# Revit family: 54-3334-001 DN1400-1800
name_source: partatom
category: Pipe Accessories
units: mm (PartAtom-declared; Revit-internal decimal feet)

## family parameters
Always vertical = No
Cut with Voids When Loaded = No
Part Type = Valve - Breaks Into
Round Connector Dimension = Use Diameter
Shared = No
Work Plane-Based = No

## types (17) — shared parameters
1 = 1 mm  [stored 0.00328084 ft]
10 = 10 mm  [stored 0.0328084 ft]
25 = 25 mm  [stored 0.082021 ft]
54-1400-33-0303100 = DN1400_ PN10_ CTC
54-1400-33-0304100 = DN1400_ PN10_ CTC
54-1400-33-1303100 = DN1400_ PN16_ CTC
54-1400-33-1304100 = DN1400_ PN16_ CTC
54-1400-34-0303100 = DN1400_ PN10_ CTO
54-1400-34-1303100 = DN1400_ PN16_ CTO
54-1600-33-0303100 = DN1600_ PN10_ CTC
54-1600-33-0304100 = DN1600_ PN10_ CTC
54-1600-33-1303100 = DN1600_ PN16_ CTC
54-1600-33-1304100 = DN1600_ PN16_ CTC
54-1600-34-0303100 = DN1600_ PN10_ CTO
54-1600-34-1303100 = DN1600_ PN16_ CTO
54-1600-34-1304100 = DN1600_ PN16_ CTO
54-1800-33-0304100 = DN1800_ PN10_ CTC
54-1800-33-1304100 = DN1800_ PN16_ CTC
54-1800-34-0304100 = DN1800_ PN10_ CTO
54-1800-34-1304100 = DN1800_ PN16_ CTO
60 = 110 mm
Bypass_W = 82 mm
Description_ = AVK GATE VALVE, FLANGED, METAL SEATED, PN10/16
H = 782 mm
Raised_dis = 5 mm  [stored 0.0164042 ft]
Rib_H1 = 600 mm
Search_table = 54-3334-001 DN1400-1800
URL product pages = https://www.avkvalves.com
sweep = 6 mm  [stored 0.019685 ft]
zero-valued in all types: Default Elevation

## per-type parameters (varying)
- 54-1400-33-0303100: ACtuator_T=33.12 mm  [stored 0.108661 ft]; ADN=1400 mm; Actuator_FLR=150 mm; Actuator_angle=133.41 mm; Actuator_dim1=90 mm; Actuator_dim2=54 mm  [stored 0.177165 ft]; BP_centre=50 mm  [stored 0.164042 ft]; BYpass_Bonnet_D1=186.77 mm; BYpass_Bonnet_D2=98.18 mm; Body_H=1435 mm; Body_L=1564.8 mm; Body_T=692.5 mm; Body_W=648 mm; Body_rib_T=18.4 mm  [stored 0.0603675 ft]; Bonnet_FL_L=1956 mm; Bonnet_FL_T=87.4 mm; Bonnet_FL_W=864 mm; Bonnet_dim1=312.96 mm; Bonnet_dim2=226.8 mm; Bonnet_dim3=2468.2 mm; Bonnet_fillet=72 mm; Bonnet_rib_L=978 mm; Bore=700 mm; Bypass_Arc=85 mm; Bypass_DN=100 mm; Bypass_Dimension=194.55 mm; Bypass_H=600 mm; Bypass_H1=60 mm  [stored 0.19685 ft]; Bypass_Location=220 mm; Bypass_R=100 mm; Bypass_R1=200 mm; Bypass_R11=130 mm; Bypass_Stem_D1=540 mm; Bypass_T=25 mm  [stored 0.082021 ft]; Bypass_Valve_Location=1102.45 mm; Bypass_cap=856.02 mm; Bypass_dis=50 mm  [stored 0.164042 ft]; Bypass_shaft=140 mm; Bypass_stem_D2=33.12 mm  [stored 0.108661 ft]; Bypass_stem_D3=52.99 mm; Bypass_valve_FL1=115.5 mm; Bypass_valve_FL2=155.93 mm; Bypass_valve_L1=320 mm; Bypass_valve_L2=116.73 mm; Bypass_valve_L3=175.1 mm; Bypass_valve_T=77 mm; Bypass_valve_W=155.64 mm; Cut_dis=43.7 mm  [stored 0.143373 ft]; DN=1400 mm; F=60 mm  [stored 0.19685 ft]; F1=27 mm  [stored 0.0885827 ft]; F2=166 mm; FL_T=46 mm  [stored 0.150919 ft]; Fillet=216 mm; H1=2870 mm; H2=885 mm; L=876 mm; OD=1675 mm; OD1=1770 mm; PN=10 mm  [stored 0.0328084 ft]; Raised_dia=1530 mm; Rib_Actual=1137.5 mm; Rib_H=1148 mm; Rib_H2=950 mm; Rib_H3=1150 mm; Rib_H4=1310 mm; Rib_L=880.2 mm; Rib_W=388.8 mm; Stem_dim=75 mm; W=2275 mm; W1=1297 mm; W_half=978 mm; bottom_rib=837.5 mm; stem_dim=55.33 mm; stem_dim1=97.5 mm; wedge_dim1=712.8 mm
- 54-1400-33-0304100: ACtuator_T=33.12 mm  [stored 0.108661 ft]; ADN=1400 mm; Actuator_FLR=175 mm; Actuator_angle=133.41 mm; Actuator_dim1=105 mm; Actuator_dim2=63 mm  [stored 0.206693 ft]; BP_centre=50 mm  [stored 0.164042 ft]; BYpass_Bonnet_D1=186.77 mm; BYpass_Bonnet_D2=98.18 mm; Body_H=1435 mm; Body_L=1564.8 mm; Body_T=692.5 mm; Body_W=648 mm; Body_rib_T=18.4 mm  [stored 0.0603675 ft]; Bonnet_FL_L=1956 mm; Bonnet_FL_T=87.4 mm; Bonnet_FL_W=864 mm; Bonnet_dim1=312.96 mm; Bonnet_dim2=226.8 mm; Bonnet_dim3=2468.2 mm; Bonnet_fillet=72 mm; Bonnet_rib_L=978 mm; Bore=700.05 mm; Bypass_Arc=85 mm; Bypass_DN=100 mm; Bypass_Dimension=194.55 mm; Bypass_H=600 mm; Bypass_H1=60 mm  [stored 0.19685 ft]; Bypass_Location=220 mm; Bypass_R=100 mm; Bypass_R1=200 mm; Bypass_R11=130 mm; Bypass_Stem_D1=540 mm; Bypass_T=25 mm  [stored 0.082021 ft]; Bypass_Valve_Location=1102.45 mm; Bypass_cap=856.02 mm; Bypass_dis=50 mm  [stored 0.164042 ft]; Bypass_shaft=140 mm; Bypass_stem_D2=33.12 mm  [stored 0.108661 ft]; Bypass_stem_D3=52.99 mm; Bypass_valve_FL1=115.5 mm; Bypass_valve_FL2=155.93 mm; Bypass_valve_L1=320 mm; Bypass_valve_L2=116.73 mm; Bypass_valve_L3=175.1 mm; Bypass_valve_T=77 mm; Bypass_valve_W=155.64 mm; Cut_dis=43.7 mm  [stored 0.143373 ft]; DN=1400.1 mm; F=70 mm; F1=31.5 mm  [stored 0.103346 ft]; F2=202 mm; FL_T=46 mm  [stored 0.150919 ft]; Fillet=216 mm; H1=2870 mm; H2=885 mm; L=876 mm; OD=1675 mm; OD1=1770 mm; PN=10 mm  [stored 0.0328084 ft]; Raised_dia=1530 mm; Rib_Actual=1137.5 mm; Rib_H=1148 mm; Rib_H2=950 mm; Rib_H3=1150 mm; Rib_H4=1310 mm; Rib_L=880.2 mm; Rib_W=388.8 mm; Stem_dim=87.5 mm; W=2275 mm; W1=1297 mm; W_half=978 mm; bottom_rib=837.5 mm; stem_dim=67.33 mm; stem_dim1=113.75 mm; wedge_dim1=712.8 mm
- 54-1400-33-1303100: ACtuator_T=43.2 mm  [stored 0.141732 ft]; ADN=1400 mm; Actuator_FLR=150 mm; Actuator_angle=133.41 mm; Actuator_dim1=90 mm; Actuator_dim2=54 mm  [stored 0.177165 ft]; BP_centre=50 mm  [stored 0.164042 ft]; BYpass_Bonnet_D1=186.77 mm; BYpass_Bonnet_D2=98.18 mm; Body_H=1435 mm; Body_L=1564.8 mm; Body_T=692.5 mm; Body_W=648 mm; Body_rib_T=24 mm  [stored 0.0787402 ft]; Bonnet_FL_L=1956 mm; Bonnet_FL_T=114 mm; Bonnet_FL_W=864 mm; Bonnet_dim1=312.96 mm; Bonnet_dim2=226.8 mm; Bonnet_dim3=2468.2 mm; Bonnet_fillet=72 mm; Bonnet_rib_L=978 mm; Bore=700.06 mm; Bypass_Arc=85 mm; Bypass_DN=100 mm; Bypass_Dimension=194.55 mm; Bypass_H=600 mm; Bypass_H1=60 mm  [stored 0.19685 ft]; Bypass_Location=220 mm; Bypass_R=100 mm; Bypass_R1=200 mm; Bypass_R11=130 mm; Bypass_Stem_D1=540 mm; Bypass_T=25 mm  [stored 0.082021 ft]; Bypass_Valve_Location=1102.45 mm; Bypass_cap=856.02 mm; Bypass_dis=50 mm  [stored 0.164042 ft]; Bypass_shaft=140 mm; Bypass_stem_D2=43.2 mm  [stored 0.141732 ft]; Bypass_stem_D3=69.12 mm; Bypass_valve_FL1=115.5 mm; Bypass_valve_FL2=155.93 mm; Bypass_valve_L1=320 mm; Bypass_valve_L2=116.73 mm; Bypass_valve_L3=175.1 mm; Bypass_valve_T=77 mm; Bypass_valve_W=155.64 mm; Cut_dis=57 mm  [stored 0.187008 ft]; DN=1400.11 mm; F=60 mm  [stored 0.19685 ft]; F1=27 mm  [stored 0.0885827 ft]; F2=166 mm; FL_T=60 mm  [stored 0.19685 ft]; Fillet=216 mm; H1=2870 mm; H2=885 mm; L=876 mm; OD=1675 mm; OD1=1770 mm; PN=16 mm  [stored 0.0524934 ft]; Raised_dia=1530 mm; Rib_Actual=1137.5 mm; Rib_H=1148 mm; Rib_H2=950 mm; Rib_H3=1150 mm; Rib_H4=1310 mm; Rib_L=880.2 mm; Rib_W=388.8 mm; Stem_dim=75 mm; W=2275 mm; W1=1297 mm; W_half=978 mm; bottom_rib=837.5 mm; stem_dim=55.33 mm; stem_dim1=97.5 mm; wedge_dim1=712.8 mm
- 54-1400-33-1304100: ACtuator_T=43.2 mm  [stored 0.141732 ft]; ADN=1400 mm; Actuator_FLR=175 mm; Actuator_angle=133.41 mm; Actuator_dim1=105 mm; Actuator_dim2=63 mm  [stored 0.206693 ft]; BP_centre=50 mm  [stored 0.164042 ft]; BYpass_Bonnet_D1=186.77 mm; BYpass_Bonnet_D2=98.18 mm; Body_H=1435 mm; Body_L=1564.8 mm; Body_T=692.5 mm; Body_W=648 mm; Body_rib_T=24 mm  [stored 0.0787402 ft]; Bonnet_FL_L=1956 mm; Bonnet_FL_T=114 mm; Bonnet_FL_W=864 mm; Bonnet_dim1=312.96 mm; Bonnet_dim2=226.8 mm; Bonnet_dim3=2468.2 mm; Bonnet_fillet=72 mm; Bonnet_rib_L=978 mm; Bore=700.06 mm; Bypass_Arc=85 mm; Bypass_DN=100 mm; Bypass_Dimension=194.55 mm; Bypass_H=600 mm; Bypass_H1=60 mm  [stored 0.19685 ft]; Bypass_Location=220 mm; Bypass_R=100 mm; Bypass_R1=200 mm; Bypass_R11=130 mm; Bypass_Stem_D1=540 mm; Bypass_T=25 mm  [stored 0.082021 ft]; Bypass_Valve_Location=1102.45 mm; Bypass_cap=856.02 mm; Bypass_dis=50 mm  [stored 0.164042 ft]; Bypass_shaft=140 mm; Bypass_stem_D2=43.2 mm  [stored 0.141732 ft]; Bypass_stem_D3=69.12 mm; Bypass_valve_FL1=115.5 mm; Bypass_valve_FL2=155.93 mm; Bypass_valve_L1=320 mm; Bypass_valve_L2=116.73 mm; Bypass_valve_L3=175.1 mm; Bypass_valve_T=77 mm; Bypass_valve_W=155.64 mm; Cut_dis=57 mm  [stored 0.187008 ft]; DN=1400.12 mm; F=70 mm; F1=31.5 mm  [stored 0.103346 ft]; F2=202 mm; FL_T=60 mm  [stored 0.19685 ft]; Fillet=216 mm; H1=2870 mm; H2=885 mm; L=876 mm; OD=1675 mm; OD1=1770 mm; PN=16 mm  [stored 0.0524934 ft]; Raised_dia=1530 mm; Rib_Actual=1137.5 mm; Rib_H=1148 mm; Rib_H2=950 mm; Rib_H3=1150 mm; Rib_H4=1310 mm; Rib_L=880.2 mm; Rib_W=388.8 mm; Stem_dim=87.5 mm; W=2275 mm; W1=1297 mm; W_half=978 mm; bottom_rib=837.5 mm; stem_dim=67.33 mm; stem_dim1=113.75 mm; wedge_dim1=712.8 mm
- 54-1400-34-0303100: ACtuator_T=33.12 mm  [stored 0.108661 ft]; ADN=1400 mm; Actuator_FLR=150 mm; Actuator_angle=133.41 mm; Actuator_dim1=90 mm; Actuator_dim2=54 mm  [stored 0.177165 ft]; BP_centre=50 mm  [stored 0.164042 ft]; BYpass_Bonnet_D1=186.77 mm; BYpass_Bonnet_D2=98.18 mm; Body_H=1435 mm; Body_L=1564.8 mm; Body_T=692.5 mm; Body_W=648 mm; Body_rib_T=18.4 mm  [stored 0.0603675 ft]; Bonnet_FL_L=1956 mm; Bonnet_FL_T=87.4 mm; Bonnet_FL_W=864 mm; Bonnet_dim1=312.96 mm; Bonnet_dim2=226.8 mm; Bonnet_dim3=2468.2 mm; Bonnet_fillet=72 mm; Bonnet_rib_L=978 mm; Bore=700.07 mm; Bypass_Arc=85 mm; Bypass_DN=100 mm; Bypass_Dimension=194.55 mm; Bypass_H=600 mm; Bypass_H1=60 mm  [stored 0.19685 ft]; Bypass_Location=220 mm; Bypass_R=100 mm; Bypass_R1=200 mm; Bypass_R11=130 mm; Bypass_Stem_D1=540 mm; Bypass_T=25 mm  [stored 0.082021 ft]; Bypass_Valve_Location=1102.45 mm; Bypass_cap=856.02 mm; Bypass_dis=50 mm  [stored 0.164042 ft]; Bypass_shaft=140 mm; Bypass_stem_D2=33.12 mm  [stored 0.108661 ft]; Bypass_stem_D3=52.99 mm; Bypass_valve_FL1=115.5 mm; Bypass_valve_FL2=155.93 mm; Bypass_valve_L1=320 mm; Bypass_valve_L2=116.73 mm; Bypass_valve_L3=175.1 mm; Bypass_valve_T=77 mm; Bypass_valve_W=155.64 mm; Cut_dis=43.7 mm  [stored 0.143373 ft]; DN=1400.13 mm; F=60 mm  [stored 0.19685 ft]; F1=27 mm  [stored 0.0885827 ft]; F2=166 mm; FL_T=46 mm  [stored 0.150919 ft]; Fillet=216 mm; H1=2870 mm; H2=885 mm; L=876 mm; OD=1675 mm; OD1=1770 mm; PN=10 mm  [stored 0.0328084 ft]; Raised_dia=1530 mm; Rib_Actual=1137.5 mm; Rib_H=1148 mm; Rib_H2=950 mm; Rib_H3=1150 mm; Rib_H4=1310 mm; Rib_L=880.2 mm; Rib_W=388.8 mm; Stem_dim=75 mm; W=2275 mm; W1=1297 mm; W_half=978 mm; bottom_rib=837.5 mm; stem_dim=55.33 mm; stem_dim1=97.5 mm; wedge_dim1=712.8 mm
- 54-1400-34-1303100: ACtuator_T=43.2 mm  [stored 0.141732 ft]; ADN=1400 mm; Actuator_FLR=150 mm; Actuator_angle=133.41 mm; Actuator_dim1=90 mm; Actuator_dim2=54 mm  [stored 0.177165 ft]; BP_centre=50 mm  [stored 0.164042 ft]; BYpass_Bonnet_D1=186.77 mm; BYpass_Bonnet_D2=98.18 mm; Body_H=1435 mm; Body_L=1564.8 mm; Body_T=692.5 mm; Body_W=648 mm; Body_rib_T=24 mm  [stored 0.0787402 ft]; Bonnet_FL_L=1956 mm; Bonnet_FL_T=114 mm; Bonnet_FL_W=864 mm; Bonnet_dim1=312.96 mm; Bonnet_dim2=226.8 mm; Bonnet_dim3=2468.2 mm; Bonnet_fillet=72 mm; Bonnet_rib_L=978 mm; Bore=700.07 mm; Bypass_Arc=85 mm; Bypass_DN=100 mm; Bypass_Dimension=194.55 mm; Bypass_H=600 mm; Bypass_H1=60 mm  [stored 0.19685 ft]; Bypass_Location=220 mm; Bypass_R=100 mm; Bypass_R1=200 mm; Bypass_R11=130 mm; Bypass_Stem_D1=540 mm; Bypass_T=25 mm  [stored 0.082021 ft]; Bypass_Valve_Location=1102.45 mm; Bypass_cap=856.02 mm; Bypass_dis=50 mm  [stored 0.164042 ft]; Bypass_shaft=140 mm; Bypass_stem_D2=43.2 mm  [stored 0.141732 ft]; Bypass_stem_D3=69.12 mm; Bypass_valve_FL1=115.5 mm; Bypass_valve_FL2=155.93 mm; Bypass_valve_L1=320 mm; Bypass_valve_L2=116.73 mm; Bypass_valve_L3=175.1 mm; Bypass_valve_T=77 mm; Bypass_valve_W=155.64 mm; Cut_dis=57 mm  [stored 0.187008 ft]; DN=1400.14 mm; F=60 mm  [stored 0.19685 ft]; F1=27 mm  [stored 0.0885827 ft]; F2=166 mm; FL_T=60 mm  [stored 0.19685 ft]; Fillet=216 mm; H1=2870 mm; H2=885 mm; L=876 mm; OD=1675 mm; OD1=1770 mm; PN=16 mm  [stored 0.0524934 ft]; Raised_dia=1530 mm; Rib_Actual=1137.5 mm; Rib_H=1148 mm; Rib_H2=950 mm; Rib_H3=1150 mm; Rib_H4=1310 mm; Rib_L=880.2 mm; Rib_W=388.8 mm; Stem_dim=75 mm; W=2275 mm; W1=1297 mm; W_half=978 mm; bottom_rib=837.5 mm; stem_dim=55.33 mm; stem_dim1=97.5 mm; wedge_dim1=712.8 mm
- 54-1600-33-0303100: ACtuator_T=35.28 mm  [stored 0.115748 ft]; ADN=1600 mm; Actuator_FLR=150 mm; Actuator_angle=141.13 mm; Actuator_dim1=90 mm; Actuator_dim2=54 mm  [stored 0.177165 ft]; BP_centre=65 mm; BYpass_Bonnet_D1=206.5 mm; BYpass_Bonnet_D2=115.58 mm; Body_H=1645.5 mm; Body_L=1832 mm; Body_T=792.5 mm; Body_W=685.5 mm; Body_rib_T=19.6 mm  [stored 0.0643045 ft]; Bonnet_FL_L=2290 mm; Bonnet_FL_T=93.1 mm; Bonnet_FL_W=914 mm; Bonnet_dim1=366.4 mm; Bonnet_dim2=239.93 mm; Bonnet_dim3=2830.26 mm; Bonnet_fillet=76.17 mm; Bonnet_rib_L=1145 mm; Bore=800 mm; Bypass_Arc=100 mm; Bypass_DN=150 mm; Bypass_Dimension=215.1 mm; Bypass_H=730 mm; Bypass_H1=73 mm; Bypass_Location=259 mm; Bypass_R=130 mm; Bypass_R1=260 mm; Bypass_R11=169 mm; Bypass_Stem_D1=657 mm; Bypass_T=35 mm  [stored 0.114829 ft]; Bypass_Valve_Location=1218.9 mm; Bypass_cap=946.44 mm; Bypass_dis=60 mm  [stored 0.19685 ft]; Bypass_shaft=150 mm; Bypass_stem_D2=35.28 mm  [stored 0.115748 ft]; Bypass_stem_D3=56.45 mm; Bypass_valve_FL1=135.98 mm; Bypass_valve_FL2=183.57 mm; Bypass_valve_L1=360 mm; Bypass_valve_L2=129.06 mm; Bypass_valve_L3=193.59 mm; Bypass_valve_T=90.65 mm; Bypass_valve_W=172.08 mm; Cut_dis=46.55 mm  [stored 0.152723 ft]; DN=1600 mm; F=60 mm  [stored 0.19685 ft]; F1=27 mm  [stored 0.0885827 ft]; F2=179 mm; FL_T=49 mm  [stored 0.160761 ft]; Fillet=228.5 mm; H1=3291 mm; H2=1060 mm; L=914 mm; OD=1915 mm; OD1=2120 mm; PN=10 mm  [stored 0.0328084 ft]; Raised_dia=1750 mm; Rib_Actual=1288.5 mm; Rib_H=1316.4 mm; Rib_H2=1100 mm; Rib_H3=1300 mm; Rib_H4=1500 mm; Rib_L=1030.5 mm; Rib_W=411.3 mm; Stem_dim=75 mm; W=2577 mm; W1=1434 mm; W_half=1143 mm; bottom_rib=957.5 mm; stem_dim=59.67 mm; stem_dim1=97.5 mm; wedge_dim1=754.05 mm
- 54-1600-33-0304100: ACtuator_T=35.28 mm  [stored 0.115748 ft]; ADN=1600 mm; Actuator_FLR=175 mm; Actuator_angle=141.13 mm; Actuator_dim1=105 mm; Actuator_dim2=63 mm  [stored 0.206693 ft]; BP_centre=65 mm; BYpass_Bonnet_D1=206.5 mm; BYpass_Bonnet_D2=115.58 mm; Body_H=1645.5 mm; Body_L=1832 mm; Body_T=792.5 mm; Body_W=685.5 mm; Body_rib_T=19.6 mm  [stored 0.0643045 ft]; Bonnet_FL_L=2290 mm; Bonnet_FL_T=93.1 mm; Bonnet_FL_W=914 mm; Bonnet_dim1=366.4 mm; Bonnet_dim2=239.93 mm; Bonnet_dim3=2830.26 mm; Bonnet_fillet=76.17 mm; Bonnet_rib_L=1145 mm; Bore=800.05 mm; Bypass_Arc=100 mm; Bypass_DN=150 mm; Bypass_Dimension=215.1 mm; Bypass_H=730 mm; Bypass_H1=73 mm; Bypass_Location=259 mm; Bypass_R=130 mm; Bypass_R1=260 mm; Bypass_R11=169 mm; Bypass_Stem_D1=657 mm; Bypass_T=35 mm  [stored 0.114829 ft]; Bypass_Valve_Location=1218.9 mm; Bypass_cap=946.44 mm; Bypass_dis=60 mm  [stored 0.19685 ft]; Bypass_shaft=150 mm; Bypass_stem_D2=35.28 mm  [stored 0.115748 ft]; Bypass_stem_D3=56.45 mm; Bypass_valve_FL1=135.98 mm; Bypass_valve_FL2=183.57 mm; Bypass_valve_L1=360 mm; Bypass_valve_L2=129.06 mm; Bypass_valve_L3=193.59 mm; Bypass_valve_T=90.65 mm; Bypass_valve_W=172.08 mm; Cut_dis=46.55 mm  [stored 0.152723 ft]; DN=1600.1 mm; F=70 mm; F1=31.5 mm  [stored 0.103346 ft]; F2=205 mm; FL_T=49 mm  [stored 0.160761 ft]; Fillet=228.5 mm; H1=3291 mm; H2=1060 mm; L=914 mm; OD=1915 mm; OD1=2120 mm; PN=10 mm  [stored 0.0328084 ft]; Raised_dia=1750 mm; Rib_Actual=1288.5 mm; Rib_H=1316.4 mm; Rib_H2=1100 mm; Rib_H3=1300 mm; Rib_H4=1500 mm; Rib_L=1030.5 mm; Rib_W=411.3 mm; Stem_dim=87.5 mm; W=2577 mm; W1=1434 mm; W_half=1143 mm; bottom_rib=957.5 mm; stem_dim=68.33 mm; stem_dim1=113.75 mm; wedge_dim1=754.05 mm
- 54-1600-33-1303100: ACtuator_T=46.8 mm  [stored 0.153543 ft]; ADN=1600 mm; Actuator_FLR=150 mm; Actuator_angle=141.13 mm; Actuator_dim1=90 mm; Actuator_dim2=54 mm  [stored 0.177165 ft]; BP_centre=65 mm; BYpass_Bonnet_D1=206.5 mm; BYpass_Bonnet_D2=115.58 mm; Body_H=1645.5 mm; Body_L=1832 mm; Body_T=792.5 mm; Body_W=685.5 mm; Body_rib_T=26 mm; Bonnet_FL_L=2290 mm; Bonnet_FL_T=123.5 mm; Bonnet_FL_W=914 mm; Bonnet_dim1=366.4 mm; Bonnet_dim2=239.93 mm; Bonnet_dim3=2830.26 mm; Bonnet_fillet=76.17 mm; Bonnet_rib_L=1145 mm; Bore=800.06 mm; Bypass_Arc=100 mm; Bypass_DN=150 mm; Bypass_Dimension=215.1 mm; Bypass_H=730 mm; Bypass_H1=73 mm; Bypass_Location=259 mm; Bypass_R=130 mm; Bypass_R1=260 mm; Bypass_R11=169 mm; Bypass_Stem_D1=657 mm; Bypass_T=35 mm  [stored 0.114829 ft]; Bypass_Valve_Location=1218.9 mm; Bypass_cap=946.44 mm; Bypass_dis=60 mm  [stored 0.19685 ft]; Bypass_shaft=150 mm; Bypass_stem_D2=46.8 mm  [stored 0.153543 ft]; Bypass_stem_D3=74.88 mm; Bypass_valve_FL1=135.98 mm; Bypass_valve_FL2=183.57 mm; Bypass_valve_L1=360 mm; Bypass_valve_L2=129.06 mm; Bypass_valve_L3=193.59 mm; Bypass_valve_T=90.65 mm; Bypass_valve_W=172.08 mm; Cut_dis=61.75 mm; DN=1600.11 mm; F=60 mm  [stored 0.19685 ft]; F1=27 mm  [stored 0.0885827 ft]; F2=179 mm; FL_T=65 mm; Fillet=228.5 mm; H1=3291 mm; H2=1060 mm; L=914 mm; OD=1915 mm; OD1=2120 mm; PN=16 mm  [stored 0.0524934 ft]; Raised_dia=1750 mm; Rib_Actual=1288.5 mm; Rib_H=1316.4 mm; Rib_H2=1100 mm; Rib_H3=1300 mm; Rib_H4=1500 mm; Rib_L=1030.5 mm; Rib_W=411.3 mm; Stem_dim=75 mm; W=2577 mm; W1=1434 mm; W_half=1143 mm; bottom_rib=957.5 mm; stem_dim=59.67 mm; stem_dim1=97.5 mm; wedge_dim1=754.05 mm
- 54-1600-33-1304100: ACtuator_T=46.8 mm  [stored 0.153543 ft]; ADN=1600 mm; Actuator_FLR=175 mm; Actuator_angle=141.13 mm; Actuator_dim1=105 mm; Actuator_dim2=63 mm  [stored 0.206693 ft]; BP_centre=65 mm; BYpass_Bonnet_D1=206.5 mm; BYpass_Bonnet_D2=115.58 mm; Body_H=1645.5 mm; Body_L=1832 mm; Body_T=792.5 mm; Body_W=685.5 mm; Body_rib_T=26 mm; Bonnet_FL_L=2290 mm; Bonnet_FL_T=123.5 mm; Bonnet_FL_W=914 mm; Bonnet_dim1=366.4 mm; Bonnet_dim2=239.93 mm; Bonnet_dim3=2830.26 mm; Bonnet_fillet=76.17 mm; Bonnet_rib_L=1145 mm; Bore=800.06 mm; Bypass_Arc=100 mm; Bypass_DN=150 mm; Bypass_Dimension=215.1 mm; Bypass_H=730 mm; Bypass_H1=73 mm; Bypass_Location=259 mm; Bypass_R=130 mm; Bypass_R1=260 mm; Bypass_R11=169 mm; Bypass_Stem_D1=657 mm; Bypass_T=35 mm  [stored 0.114829 ft]; Bypass_Valve_Location=1218.9 mm; Bypass_cap=946.44 mm; Bypass_dis=60 mm  [stored 0.19685 ft]; Bypass_shaft=150 mm; Bypass_stem_D2=46.8 mm  [stored 0.153543 ft]; Bypass_stem_D3=74.88 mm; Bypass_valve_FL1=135.98 mm; Bypass_valve_FL2=183.57 mm; Bypass_valve_L1=360 mm; Bypass_valve_L2=129.06 mm; Bypass_valve_L3=193.59 mm; Bypass_valve_T=90.65 mm; Bypass_valve_W=172.08 mm; Cut_dis=61.75 mm; DN=1600.12 mm; F=70 mm; F1=31.5 mm  [stored 0.103346 ft]; F2=205 mm; FL_T=65 mm; Fillet=228.5 mm; H1=3291 mm; H2=1060 mm; L=914 mm; OD=1915 mm; OD1=2120 mm; PN=16 mm  [stored 0.0524934 ft]; Raised_dia=1750 mm; Rib_Actual=1288.5 mm; Rib_H=1316.4 mm; Rib_H2=1100 mm; Rib_H3=1300 mm; Rib_H4=1500 mm; Rib_L=1030.5 mm; Rib_W=411.3 mm; Stem_dim=87.5 mm; W=2577 mm; W1=1434 mm; W_half=1143 mm; bottom_rib=957.5 mm; stem_dim=68.33 mm; stem_dim1=113.75 mm; wedge_dim1=754.05 mm
- 54-1600-34-0303100: ACtuator_T=35.28 mm  [stored 0.115748 ft]; ADN=1600 mm; Actuator_FLR=150 mm; Actuator_angle=141.13 mm; Actuator_dim1=90 mm; Actuator_dim2=54 mm  [stored 0.177165 ft]; BP_centre=65 mm; BYpass_Bonnet_D1=206.5 mm; BYpass_Bonnet_D2=115.58 mm; Body_H=1645.5 mm; Body_L=1832 mm; Body_T=792.5 mm; Body_W=685.5 mm; Body_rib_T=19.6 mm  [stored 0.0643045 ft]; Bonnet_FL_L=2290 mm; Bonnet_FL_T=93.1 mm; Bonnet_FL_W=914 mm; Bonnet_dim1=366.4 mm; Bonnet_dim2=239.93 mm; Bonnet_dim3=2830.26 mm; Bonnet_fillet=76.17 mm; Bonnet_rib_L=1145 mm; Bore=800.07 mm; Bypass_Arc=100 mm; Bypass_DN=150 mm; Bypass_Dimension=215.1 mm; Bypass_H=730 mm; Bypass_H1=73 mm; Bypass_Location=259 mm; Bypass_R=130 mm; Bypass_R1=260 mm; Bypass_R11=169 mm; Bypass_Stem_D1=657 mm; Bypass_T=35 mm  [stored 0.114829 ft]; Bypass_Valve_Location=1218.9 mm; Bypass_cap=946.44 mm; Bypass_dis=60 mm  [stored 0.19685 ft]; Bypass_shaft=150 mm; Bypass_stem_D2=35.28 mm  [stored 0.115748 ft]; Bypass_stem_D3=56.45 mm; Bypass_valve_FL1=135.98 mm; Bypass_valve_FL2=183.57 mm; Bypass_valve_L1=360 mm; Bypass_valve_L2=129.06 mm; Bypass_valve_L3=193.59 mm; Bypass_valve_T=90.65 mm; Bypass_valve_W=172.08 mm; Cut_dis=46.55 mm  [stored 0.152723 ft]; DN=1600.13 mm; F=60 mm  [stored 0.19685 ft]; F1=27 mm  [stored 0.0885827 ft]; F2=179 mm; FL_T=49 mm  [stored 0.160761 ft]; Fillet=228.5 mm; H1=3291 mm; H2=1060 mm; L=914 mm; OD=1915 mm; OD1=2120 mm; PN=10 mm  [stored 0.0328084 ft]; Raised_dia=1750 mm; Rib_Actual=1288.5 mm; Rib_H=1316.4 mm; Rib_H2=1100 mm; Rib_H3=1300 mm; Rib_H4=1500 mm; Rib_L=1030.5 mm; Rib_W=411.3 mm; Stem_dim=75 mm; W=2577 mm; W1=1434 mm; W_half=1143 mm; bottom_rib=957.5 mm; stem_dim=59.67 mm; stem_dim1=97.5 mm; wedge_dim1=754.05 mm
- 54-1600-34-1303100: ACtuator_T=46.8 mm  [stored 0.153543 ft]; ADN=1600 mm; Actuator_FLR=150 mm; Actuator_angle=141.13 mm; Actuator_dim1=90 mm; Actuator_dim2=54 mm  [stored 0.177165 ft]; BP_centre=65 mm; BYpass_Bonnet_D1=206.5 mm; BYpass_Bonnet_D2=115.58 mm; Body_H=1645.5 mm; Body_L=1832 mm; Body_T=792.5 mm; Body_W=685.5 mm; Body_rib_T=26 mm; Bonnet_FL_L=2290 mm; Bonnet_FL_T=123.5 mm; Bonnet_FL_W=914 mm; Bonnet_dim1=366.4 mm; Bonnet_dim2=239.93 mm; Bonnet_dim3=2830.26 mm; Bonnet_fillet=76.17 mm; Bonnet_rib_L=1145 mm; Bore=800.07 mm; Bypass_Arc=100 mm; Bypass_DN=150 mm; Bypass_Dimension=215.1 mm; Bypass_H=730 mm; Bypass_H1=73 mm; Bypass_Location=259 mm; Bypass_R=130 mm; Bypass_R1=260 mm; Bypass_R11=169 mm; Bypass_Stem_D1=657 mm; Bypass_T=35 mm  [stored 0.114829 ft]; Bypass_Valve_Location=1218.9 mm; Bypass_cap=946.44 mm; Bypass_dis=60 mm  [stored 0.19685 ft]; Bypass_shaft=150 mm; Bypass_stem_D2=46.8 mm  [stored 0.153543 ft]; Bypass_stem_D3=74.88 mm; Bypass_valve_FL1=135.98 mm; Bypass_valve_FL2=183.57 mm; Bypass_valve_L1=360 mm; Bypass_valve_L2=129.06 mm; Bypass_valve_L3=193.59 mm; Bypass_valve_T=90.65 mm; Bypass_valve_W=172.08 mm; Cut_dis=61.75 mm; DN=1600.14 mm; F=60 mm  [stored 0.19685 ft]; F1=27 mm  [stored 0.0885827 ft]; F2=179 mm; FL_T=65 mm; Fillet=228.5 mm; H1=3291 mm; H2=1060 mm; L=914 mm; OD=1915 mm; OD1=2120 mm; PN=16 mm  [stored 0.0524934 ft]; Raised_dia=1750 mm; Rib_Actual=1288.5 mm; Rib_H=1316.4 mm; Rib_H2=1100 mm; Rib_H3=1300 mm; Rib_H4=1500 mm; Rib_L=1030.5 mm; Rib_W=411.3 mm; Stem_dim=75 mm; W=2577 mm; W1=1434 mm; W_half=1143 mm; bottom_rib=957.5 mm; stem_dim=59.67 mm; stem_dim1=97.5 mm; wedge_dim1=754.05 mm
- 54-1600-34-1304100: ACtuator_T=46.8 mm  [stored 0.153543 ft]; ADN=1600 mm; Actuator_FLR=175 mm; Actuator_angle=141.13 mm; Actuator_dim1=105 mm; Actuator_dim2=63 mm  [stored 0.206693 ft]; BP_centre=65 mm; BYpass_Bonnet_D1=206.5 mm; BYpass_Bonnet_D2=115.58 mm; Body_H=1645.5 mm; Body_L=1832 mm; Body_T=792.5 mm; Body_W=685.5 mm; Body_rib_T=26 mm; Bonnet_FL_L=2290 mm; Bonnet_FL_T=123.5 mm; Bonnet_FL_W=914 mm; Bonnet_dim1=366.4 mm; Bonnet_dim2=239.93 mm; Bonnet_dim3=2830.26 mm; Bonnet_fillet=76.17 mm; Bonnet_rib_L=1145 mm; Bore=800.08 mm; Bypass_Arc=100 mm; Bypass_DN=150 mm; Bypass_Dimension=215.1 mm; Bypass_H=730 mm; Bypass_H1=73 mm; Bypass_Location=259 mm; Bypass_R=130 mm; Bypass_R1=260 mm; Bypass_R11=169 mm; Bypass_Stem_D1=657 mm; Bypass_T=35 mm  [stored 0.114829 ft]; Bypass_Valve_Location=1218.9 mm; Bypass_cap=946.44 mm; Bypass_dis=60 mm  [stored 0.19685 ft]; Bypass_shaft=150 mm; Bypass_stem_D2=46.8 mm  [stored 0.153543 ft]; Bypass_stem_D3=74.88 mm; Bypass_valve_FL1=135.98 mm; Bypass_valve_FL2=183.57 mm; Bypass_valve_L1=360 mm; Bypass_valve_L2=129.06 mm; Bypass_valve_L3=193.59 mm; Bypass_valve_T=90.65 mm; Bypass_valve_W=172.08 mm; Cut_dis=61.75 mm; DN=1600.15 mm; F=70 mm; F1=31.5 mm  [stored 0.103346 ft]; F2=205 mm; FL_T=65 mm; Fillet=228.5 mm; H1=3291 mm; H2=1060 mm; L=914 mm; OD=1915 mm; OD1=2120 mm; PN=16 mm  [stored 0.0524934 ft]; Raised_dia=1750 mm; Rib_Actual=1288.5 mm; Rib_H=1316.4 mm; Rib_H2=1100 mm; Rib_H3=1300 mm; Rib_H4=1500 mm; Rib_L=1030.5 mm; Rib_W=411.3 mm; Stem_dim=87.5 mm; W=2577 mm; W1=1434 mm; W_half=1143 mm; bottom_rib=957.5 mm; stem_dim=68.33 mm; stem_dim1=113.75 mm; wedge_dim1=754.05 mm
- 54-1800-33-0304100: ACtuator_T=37.44 mm  [stored 0.122835 ft]; ADN=1800 mm; Actuator_FLR=175 mm; Actuator_angle=156.88 mm; Actuator_dim1=105 mm; Actuator_dim2=63 mm  [stored 0.206693 ft]; BP_centre=80 mm; BYpass_Bonnet_D1=230.54 mm; BYpass_Bonnet_D2=115.58 mm; Body_H=1829.5 mm; Body_L=1910.4 mm; Body_T=892.5 mm; Body_W=762 mm; Body_rib_T=20.8 mm  [stored 0.0682415 ft]; Bonnet_FL_L=2388 mm; Bonnet_FL_T=98.8 mm; Bonnet_FL_W=1016 mm; Bonnet_dim1=382.08 mm; Bonnet_dim2=266.7 mm; Bonnet_dim3=3146.74 mm; Bonnet_fillet=84.67 mm; Bonnet_rib_L=1194 mm; Bore=900 mm; Bypass_Arc=105 mm; Bypass_DN=200 mm; Bypass_Dimension=240.15 mm; Bypass_H=820 mm; Bypass_H1=82 mm; Bypass_Location=259 mm; Bypass_R=160 mm; Bypass_R1=320 mm; Bypass_R11=208 mm; Bypass_Stem_D1=738 mm; Bypass_T=40 mm  [stored 0.131234 ft]; Bypass_Valve_Location=1360.85 mm; Bypass_cap=1056.66 mm; Bypass_dis=60 mm  [stored 0.19685 ft]; Bypass_shaft=140 mm; Bypass_stem_D2=37.44 mm  [stored 0.122835 ft]; Bypass_stem_D3=59.9 mm; Bypass_valve_FL1=135.98 mm; Bypass_valve_FL2=183.57 mm; Bypass_valve_L1=390 mm; Bypass_valve_L2=144.09 mm; Bypass_valve_L3=216.14 mm; Bypass_valve_T=90.65 mm; Bypass_valve_W=192.12 mm; Cut_dis=49.4 mm  [stored 0.162073 ft]; DN=1800 mm; F=70 mm; F1=31.5 mm  [stored 0.103346 ft]; F2=208 mm; FL_T=52 mm; Fillet=254 mm; H1=3659 mm; H2=1180 mm; L=1067 mm; OD=2115 mm; OD1=2360 mm; PN=10 mm  [stored 0.0328084 ft]; Raised_dia=1950 mm; Rib_Actual=1397.5 mm; Rib_H=1463.6 mm; Rib_H2=1300 mm; Rib_H3=1500 mm; Rib_H4=1700 mm; Rib_L=1074.6 mm; Rib_W=457.2 mm; Stem_dim=87.5 mm; W=2795 mm; W1=1601 mm; W_half=1194 mm; bottom_rib=1057.5 mm; stem_dim=69.33 mm; stem_dim1=113.75 mm; wedge_dim1=838.2 mm
- 54-1800-33-1304100: ACtuator_T=50.4 mm  [stored 0.165354 ft]; ADN=1800 mm; Actuator_FLR=175 mm; Actuator_angle=156.88 mm; Actuator_dim1=105 mm; Actuator_dim2=63 mm  [stored 0.206693 ft]; BP_centre=80 mm; BYpass_Bonnet_D1=230.54 mm; BYpass_Bonnet_D2=115.58 mm; Body_H=1829.5 mm; Body_L=1910.4 mm; Body_T=892.5 mm; Body_W=762 mm; Body_rib_T=28 mm  [stored 0.0918635 ft]; Bonnet_FL_L=2388 mm; Bonnet_FL_T=133 mm; Bonnet_FL_W=1016 mm; Bonnet_dim1=382.08 mm; Bonnet_dim2=266.7 mm; Bonnet_dim3=3146.74 mm; Bonnet_fillet=84.67 mm; Bonnet_rib_L=1194 mm; Bore=900.05 mm; Bypass_Arc=105 mm; Bypass_DN=200 mm; Bypass_Dimension=240.15 mm; Bypass_H=820 mm; Bypass_H1=82 mm; Bypass_Location=259 mm; Bypass_R=160 mm; Bypass_R1=320 mm; Bypass_R11=208 mm; Bypass_Stem_D1=738 mm; Bypass_T=40 mm  [stored 0.131234 ft]; Bypass_Valve_Location=1360.85 mm; Bypass_cap=1056.66 mm; Bypass_dis=60 mm  [stored 0.19685 ft]; Bypass_shaft=140 mm; Bypass_stem_D2=50.4 mm  [stored 0.165354 ft]; Bypass_stem_D3=80.64 mm; Bypass_valve_FL1=135.98 mm; Bypass_valve_FL2=183.57 mm; Bypass_valve_L1=390 mm; Bypass_valve_L2=144.09 mm; Bypass_valve_L3=216.14 mm; Bypass_valve_T=90.65 mm; Bypass_valve_W=192.12 mm; Cut_dis=66.5 mm; DN=1800.1 mm; F=70 mm; F1=31.5 mm  [stored 0.103346 ft]; F2=208 mm; FL_T=70 mm; Fillet=254 mm; H1=3659 mm; H2=1180 mm; L=1067 mm; OD=2115 mm; OD1=2360 mm; PN=16 mm  [stored 0.0524934 ft]; Raised_dia=1950 mm; Rib_Actual=1397.5 mm; Rib_H=1463.6 mm; Rib_H2=1300 mm; Rib_H3=1500 mm; Rib_H4=1700 mm; Rib_L=1074.6 mm; Rib_W=457.2 mm; Stem_dim=87.5 mm; W=2795 mm; W1=1601 mm; W_half=1194 mm; bottom_rib=1057.5 mm; stem_dim=69.33 mm; stem_dim1=113.75 mm; wedge_dim1=838.2 mm
- 54-1800-34-0304100: ACtuator_T=37.44 mm  [stored 0.122835 ft]; ADN=1800 mm; Actuator_FLR=175 mm; Actuator_angle=156.88 mm; Actuator_dim1=105 mm; Actuator_dim2=63 mm  [stored 0.206693 ft]; BP_centre=80 mm; BYpass_Bonnet_D1=230.54 mm; BYpass_Bonnet_D2=115.58 mm; Body_H=1829.5 mm; Body_L=1910.4 mm; Body_T=892.5 mm; Body_W=762 mm; Body_rib_T=20.8 mm  [stored 0.0682415 ft]; Bonnet_FL_L=2388 mm; Bonnet_FL_T=98.8 mm; Bonnet_FL_W=1016 mm; Bonnet_dim1=382.08 mm; Bonnet_dim2=266.7 mm; Bonnet_dim3=3146.74 mm; Bonnet_fillet=84.67 mm; Bonnet_rib_L=1194 mm; Bore=900.06 mm; Bypass_Arc=105 mm; Bypass_DN=200 mm; Bypass_Dimension=240.15 mm; Bypass_H=820 mm; Bypass_H1=82 mm; Bypass_Location=259 mm; Bypass_R=160 mm; Bypass_R1=320 mm; Bypass_R11=208 mm; Bypass_Stem_D1=738 mm; Bypass_T=40 mm  [stored 0.131234 ft]; Bypass_Valve_Location=1360.85 mm; Bypass_cap=1056.66 mm; Bypass_dis=60 mm  [stored 0.19685 ft]; Bypass_shaft=140 mm; Bypass_stem_D2=37.44 mm  [stored 0.122835 ft]; Bypass_stem_D3=59.9 mm; Bypass_valve_FL1=135.98 mm; Bypass_valve_FL2=183.57 mm; Bypass_valve_L1=390 mm; Bypass_valve_L2=144.09 mm; Bypass_valve_L3=216.14 mm; Bypass_valve_T=90.65 mm; Bypass_valve_W=192.12 mm; Cut_dis=49.4 mm  [stored 0.162073 ft]; DN=1800.11 mm; F=70 mm; F1=31.5 mm  [stored 0.103346 ft]; F2=208 mm; FL_T=52 mm; Fillet=254 mm; H1=3659 mm; H2=1180 mm; L=1067 mm; OD=2115 mm; OD1=2360 mm; PN=10 mm  [stored 0.0328084 ft]; Raised_dia=1950 mm; Rib_Actual=1397.5 mm; Rib_H=1463.6 mm; Rib_H2=1300 mm; Rib_H3=1500 mm; Rib_H4=1700 mm; Rib_L=1074.6 mm; Rib_W=457.2 mm; Stem_dim=87.5 mm; W=2795 mm; W1=1601 mm; W_half=1194 mm; bottom_rib=1057.5 mm; stem_dim=69.33 mm; stem_dim1=113.75 mm; wedge_dim1=838.2 mm
- 54-1800-34-1304100: ACtuator_T=50.4 mm  [stored 0.165354 ft]; ADN=1800 mm; Actuator_FLR=175 mm; Actuator_angle=156.88 mm; Actuator_dim1=105 mm; Actuator_dim2=63 mm  [stored 0.206693 ft]; BP_centre=80 mm; BYpass_Bonnet_D1=230.54 mm; BYpass_Bonnet_D2=115.58 mm; Body_H=1829.5 mm; Body_L=1910.4 mm; Body_T=892.5 mm; Body_W=762 mm; Body_rib_T=28 mm  [stored 0.0918635 ft]; Bonnet_FL_L=2388 mm; Bonnet_FL_T=133 mm; Bonnet_FL_W=1016 mm; Bonnet_dim1=382.08 mm; Bonnet_dim2=266.7 mm; Bonnet_dim3=3146.74 mm; Bonnet_fillet=84.67 mm; Bonnet_rib_L=1194 mm; Bore=900.06 mm; Bypass_Arc=105 mm; Bypass_DN=200 mm; Bypass_Dimension=240.15 mm; Bypass_H=820 mm; Bypass_H1=82 mm; Bypass_Location=259 mm; Bypass_R=160 mm; Bypass_R1=320 mm; Bypass_R11=208 mm; Bypass_Stem_D1=738 mm; Bypass_T=40 mm  [stored 0.131234 ft]; Bypass_Valve_Location=1360.85 mm; Bypass_cap=1056.66 mm; Bypass_dis=60 mm  [stored 0.19685 ft]; Bypass_shaft=140 mm; Bypass_stem_D2=50.4 mm  [stored 0.165354 ft]; Bypass_stem_D3=80.64 mm; Bypass_valve_FL1=135.98 mm; Bypass_valve_FL2=183.57 mm; Bypass_valve_L1=390 mm; Bypass_valve_L2=144.09 mm; Bypass_valve_L3=216.14 mm; Bypass_valve_T=90.65 mm; Bypass_valve_W=192.12 mm; Cut_dis=66.5 mm; DN=1800.12 mm; F=70 mm; F1=31.5 mm  [stored 0.103346 ft]; F2=208 mm; FL_T=70 mm; Fillet=254 mm; H1=3659 mm; H2=1180 mm; L=1067 mm; OD=2115 mm; OD1=2360 mm; PN=16 mm  [stored 0.0524934 ft]; Raised_dia=1950 mm; Rib_Actual=1397.5 mm; Rib_H=1463.6 mm; Rib_H2=1300 mm; Rib_H3=1500 mm; Rib_H4=1700 mm; Rib_L=1074.6 mm; Rib_W=457.2 mm; Stem_dim=87.5 mm; W=2795 mm; W1=1601 mm; W_half=1194 mm; bottom_rib=1057.5 mm; stem_dim=69.33 mm; stem_dim1=113.75 mm; wedge_dim1=838.2 mm

note: [stored X ft] marks values corroborated as IEEE doubles in the binary element streams (Revit-internal decimal feet)

## geometry (parser evidence)
native form markers: Sweep x4
no freeform markers — native parametric forms only
